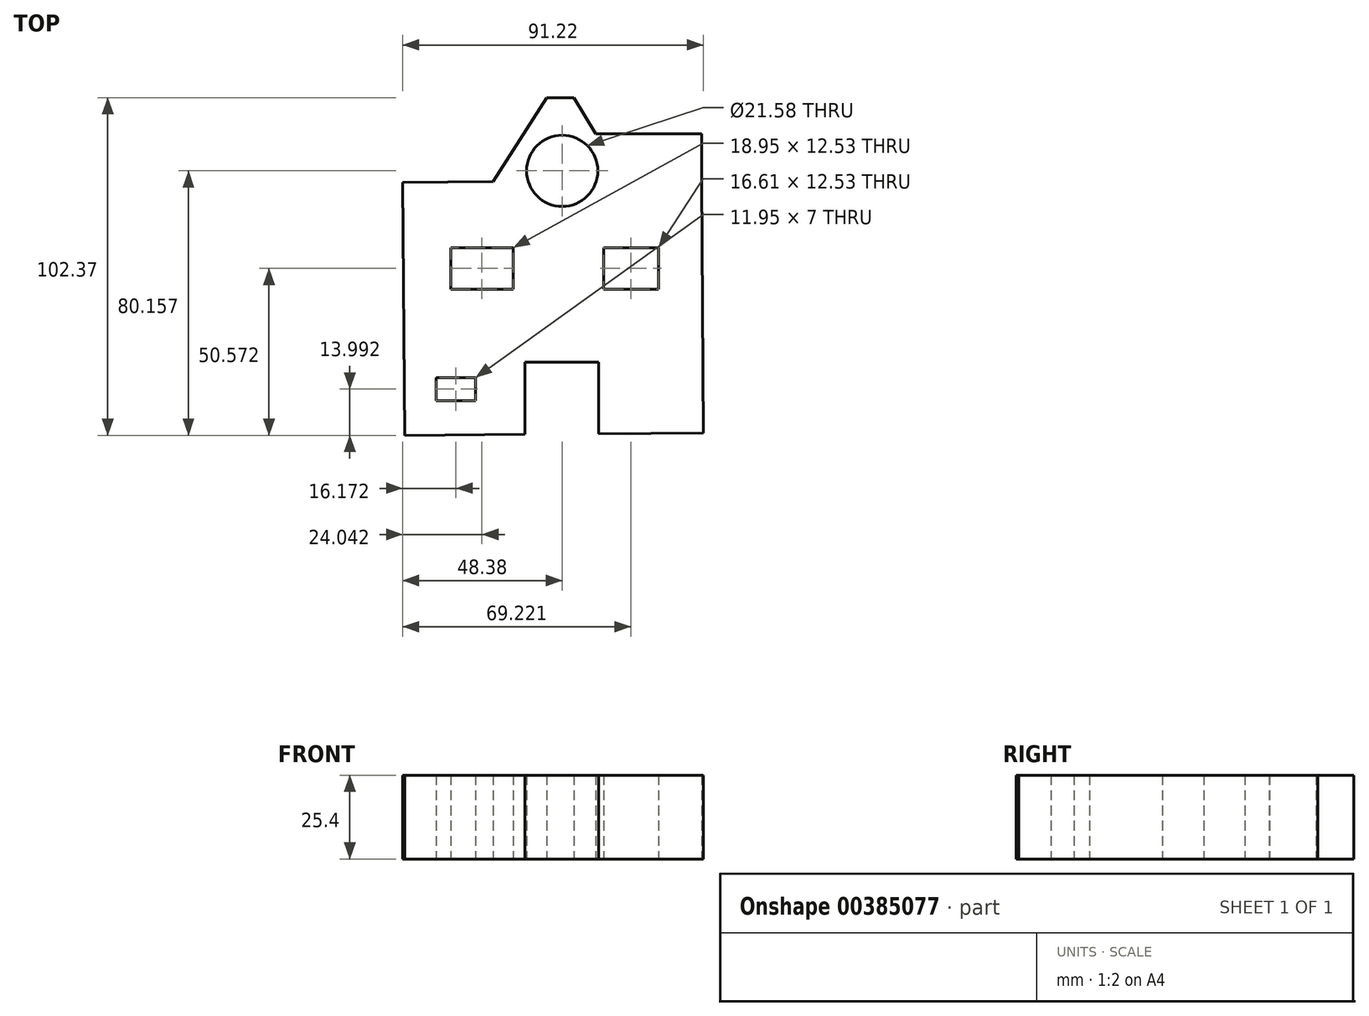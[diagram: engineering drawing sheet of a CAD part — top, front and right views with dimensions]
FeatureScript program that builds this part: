
annotation { "Feature Type Name" : "Feature", "Feature Type Description" : "" }
export const myFeature = defineFeature(function(context is Context, id is Id, definition is map)
    precondition{}
    {
        {
            var Q0;
            Q0=qCreatedBy(makeId("Top.planeOp"),FACE);
            var sketch = newSketch(context, id + "F0", { "sketchPlane" : qUnion([Q0])});
            skLineSegment(sketch, "E0", {"start": v(-48.38, 50.28) * mm, "end": v(-47.8, -26.38) * mm});
            skLineSegment(sketch, "E1", {"start": v(-47.8, -26.38) * mm, "end": v(42.84, -25.69) * mm});
            skLineSegment(sketch, "E2", {"start": v(42.84, -25.69) * mm, "end": v(42.26, 50.88) * mm});
            skPoint(sketch, "E3.end.orphan", {"position": v(10.78, 47.07) * mm});
            skPoint(sketch, "E4.end.orphan", {"position": v(0, 67.48) * mm});
            skPoint(sketch, "E4.start.orphan", {"position": v(-8.16, 47.07) * mm});
            skPoint(sketch, "E5.start.orphan", {"position": v(-47.8, 30.46) * mm});
            skLineSegment(sketch, "E6", {"start": v(-48.38, 50.28) * mm, "end": v(-21, 50.49) * mm});
            skLineSegment(sketch, "E7", {"start": v(-48.38, 50.28) * mm, "end": v(-37.6, 64.85) * mm});
            skLineSegment(sketch, "E8", {"start": v(-37.6, 64.85) * mm, "end": v(-11.65, 65.05) * mm});
            skLineSegment(sketch, "E9", {"start": v(-21, 50.49) * mm, "end": v(-4.66, 75.93) * mm});
            skLineSegment(sketch, "E10", {"start": v(-4.66, 75.93) * mm, "end": v(3.5, 76) * mm});
            skLineSegment(sketch, "E11", {"start": v(3.5, 76) * mm, "end": v(10.13, 65.05) * mm});
            skLineSegment(sketch, "E12", {"start": v(42.26, 65.05) * mm, "end": v(10.13, 65.05) * mm});
            skLineSegment(sketch, "E13", {"start": v(10.13, 65.05) * mm, "end": v(42.26, 65.05) * mm});
            skLineSegment(sketch, "E14", {"start": v(42.26, 50.88) * mm, "end": v(42.26, 65.05) * mm});
            skPoint(sketch, "E15.orphan", {"position": v(18.95, 50.49) * mm});
            skCircle(sketch, "E16", {"center": v(0, 53.78) * mm, "radius": 10.79 * mm});
            skLineSegment(sketch, "E17", {"start": v(0, 64.57) * mm, "end": v(0, 42.99) * mm});
            skLineSegment(sketch, "E18", {"start": v(-10.79, 53.78) * mm, "end": v(10.79, 53.78) * mm});
            skLineSegment(sketch, "E19.bottom", {"start": v(-11.37, -26.1) * mm, "end": v(11.08, -26.1) * mm});
            skLineSegment(sketch, "E19.top", {"start": v(-11.37, -4.23) * mm, "end": v(11.08, -4.23) * mm});
            skLineSegment(sketch, "E19.left", {"start": v(-11.37, -26.1) * mm, "end": v(-11.37, -4.23) * mm});
            skLineSegment(sketch, "E19.right", {"start": v(11.08, -26.1) * mm, "end": v(11.08, -4.23) * mm});
            skLineSegment(sketch, "E20.bottom", {"start": v(-38.18, -8.9) * mm, "end": v(-26.23, -8.9) * mm});
            skLineSegment(sketch, "E20.top", {"start": v(-38.18, -15.89) * mm, "end": v(-26.23, -15.89) * mm});
            skLineSegment(sketch, "E20.left", {"start": v(-38.18, -8.9) * mm, "end": v(-38.18, -15.89) * mm});
            skLineSegment(sketch, "E20.right", {"start": v(-26.23, -8.9) * mm, "end": v(-26.23, -15.89) * mm});
            skLineSegment(sketch, "E21.bottom", {"start": v(12.53, 30.46) * mm, "end": v(29.15, 30.46) * mm});
            skLineSegment(sketch, "E21.top", {"start": v(12.53, 17.93) * mm, "end": v(29.15, 17.93) * mm});
            skLineSegment(sketch, "E21.left", {"start": v(12.53, 30.46) * mm, "end": v(12.53, 17.93) * mm});
            skLineSegment(sketch, "E21.right", {"start": v(29.15, 30.46) * mm, "end": v(29.15, 17.93) * mm});
            skPoint(sketch, "E22.oppositeSnap0", {"position": v(20.84, 17.93) * mm});
            skLineSegment(sketch, "E22.bottom", {"start": v(-14.87, 30.46) * mm, "end": v(-33.81, 30.46) * mm});
            skLineSegment(sketch, "E22.top", {"start": v(-14.87, 17.93) * mm, "end": v(-33.81, 17.93) * mm});
            skLineSegment(sketch, "E22.left", {"start": v(-14.87, 30.46) * mm, "end": v(-14.87, 17.93) * mm});
            skLineSegment(sketch, "E22.right", {"start": v(-33.81, 30.46) * mm, "end": v(-33.81, 17.93) * mm});
            skLineSegment(sketch, "E23", {"start": v(-24.34, 30.46) * mm, "end": v(-24.34, 17.93) * mm});
            skLineSegment(sketch, "E24", {"start": v(-33.81, 24.2) * mm, "end": v(-14.87, 24.2) * mm});
            skLineSegment(sketch, "E25", {"start": v(12.53, 24.2) * mm, "end": v(29.15, 24.2) * mm});
            skLineSegment(sketch, "E26", {"start": v(20.84, 30.46) * mm, "end": v(20.84, 17.93) * mm});
            skLineSegment(sketch, "E27", {"start": v(-0.14, -4.23) * mm, "end": v(-0.14, -26.02) * mm});
            skSolve(sketch);
        }
        {
            var Q0;
            {var subQ15=sQuery(id+"F0.wireOp",EDGE,"E0");Q0=makeQuery(id+"F0.imprint","IMPRINT",FACE,{"disambiguationData":[TD([[makeQuery(id+"F0.imprint","IMPRINT",EDGE,{"derivedFrom":subQ15}),1.0]])]});}
            extrude(context, id + "F1", {"entities" : qUnion([Q0]), "depth" : 25.4 * mm});
        }
    });
